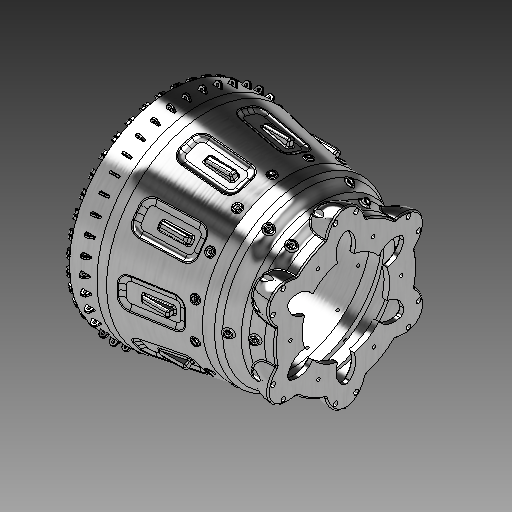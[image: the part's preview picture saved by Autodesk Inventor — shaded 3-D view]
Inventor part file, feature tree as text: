
AUTODESK INVENTOR PART (.ipt)
format: ipt  version: 2019 (Build 230136000, 136)  size: 8,577,024 bytes
history: native  units: mm
features: sketch x16, fillet x11, extrude x9, pattern_circular x9, hole x8, plane x7, other x6, revolve x1, sweep x1, delete_face x1, mirror x1, emboss x1, chamfer x1, projected_geometry x1
ambient origin geometry x8: Origin, YZ Plane, XZ Plane, XY Plane, X Axis, Y Axis, Z Axis, Center Point
bodies: Solid2 (feature_tree)
feature tree (73):
  other  "Blocks"
  sketch  "Sketch2"  dims[d2=6.0mm d3=12.566371mm]
  revolve  "Revolution1"  [1 undecoded]
  extrude  "Extrusion1"  Depth=12.0mm
  sketch  "Sketch22"  dims[d66=-6.1mm d67=4.75mm d68=0.0mm d69=-6.716mm d70=3.0mm d71=0.0mm]
  sketch  "Sketch23"  dims[d76=400.0mm d77=360.0deg d79=-139.973mm d80=40.0mm]
  sweep  "Sweep2"
  delete_face  "Delete Face7"
  plane  "Work Plane29"
  sketch  "Sketch15"  dims[d30=8.0mm d31=0.0mm]
  extrude  "Extrusion10"  Depth=121.0mm
  hole  "Hole6"  [1 undecoded]
  hole  "Hole7"  [1 undecoded]
  fillet  "Fillet14"  Radius=98.0mm
  pattern_circular  "Circular Pattern1"  Count=6 Angle=360.0deg
  plane  "Work Plane1"
  extrude  "Extrusion2"  Depth=3.0mm TaperAngle=0.0deg
  fillet  "Fillet1"  Radius=4.0mm
  pattern_circular  "Circular Pattern2"  Count=40 Angle=360.0deg
  sketch  "Sketch8"  dims[d9=16.0mm d10=121.0mm]
  plane  "Work Plane5"
  plane  "Work Plane6"
  extrude  "Extrusion4"  Depth=3.0mm TaperAngle=0.0deg
  extrude  "Extrusion3"  [1 undecoded]
  fillet  "Fillet18"  Radius=40.0mm
  pattern_circular  "Circular Pattern4"  [2 undecoded]
  mirror  "Mirror3"
  sketch  "Sketch11"  dims[d17=29.779484mm d18=6.0mm d19=98.0mm]
  plane  "Work Plane10"
  emboss  "Emboss3"
  fillet  "Fillet3"  Radius=2.0mm
  fillet  "Fillet4"  Radius=2.0mm
  pattern_circular  "Circular Pattern14"  [2 undecoded]
  plane  "Work Plane9"
  sketch  "Sketch9"  dims[d11=33.5mm d12=75.0mm]
  extrude  "Extrusion6"  Depth=10.0mm
  fillet  "Fillet20"  Radius=2.0mm
  pattern_circular  "Circular Pattern6"  [2 undecoded]
  hole  "HolePlaneOnSideFace"  [1 undecoded]
  fillet  "Fillet21"  Radius=2.0mm
  extrude  "Extrusion7"  Depth=10.0mm TaperAngle=0.0deg
  hole  "HolePlane2"  [1 undecoded]
  hole  "Hole2"  [1 undecoded]
  fillet  "Fillet6"  Radius=30.0mm
  pattern_circular  "Circular Pattern7"  [2 undecoded]
  sketch  "Sketch19"  dims[d48=0.0mm d49=3.0mm d50=0.0mm d51=4.0mm]
  other  "BottonExtrudePlane1"
  extrude  "Extrusion8"  [1 undecoded]
  other  "BottomHolePlane1"
  hole  "Hole4"  [1 undecoded]
  fillet  "Fillet7"  [1 undecoded]
  pattern_circular  "Circular Pattern8"  [2 undecoded]
  other  "MiddleExtrudePlane"
  extrude  "Extrusion9"  Depth=10.0mm TaperAngle=0.0deg
  fillet  "Fillet8"  Radius=0.715mm
  other  "MiddleHolePlane"
  hole  "Hole5"  [1 undecoded]
  pattern_circular  "Circular Pattern9"  [2 undecoded]
  hole  "Hole9"  [1 undecoded]
  pattern_circular  "Circular Pattern13"  [2 undecoded]
  fillet  "Fillet15"  Radius=10.0mm
  plane  "Work Plane42"
  sketch  "Sketch31"  dims[d81=10.0mm]
  chamfer  "Chamfer1"  Distance=3.0mm
  sketch  "Sketch4"  dims[d5=16.0mm d6=12.0mm]
  sketch  "Sketch6"  dims[d7=16.0mm d8=15.5mm]
  sketch  "Sketch12"  dims[d20=90.0deg]
  sketch  "Sketch17"  dims[d38=32.0mm d43=60.0mm d44=360.0deg]
  sketch  "Sketch20"  dims[d52=5.0mm]
  sketch  "Sketch21"  dims[d53=0.5mm d54=400.0mm d55=360.0deg]
  other  "Block1"
  sketch  "Sketch32"  dims[d82=2.0mm d83=2.0mm d84=2.0mm d85=2.0mm d86=2.0mm d87=2.0mm d88=2.0mm d89=2.0mm d95=10.0mm d96=2.0mm d103=3.0mm d104=0.0mm d105=100.0mm d106=360.0deg d108=2.8mm d111=30.0mm d113=6.0mm d114=-11.0mm d131=4.107mm d132=0.0mm d133=-131.011mm d135=11.0mm d137=3.0mm d138=0.0mm d149=10.0mm d150=10.0mm d141=4.117mm d142=6.0mm d143=7.53mm d144=2.0mm d145=90.0deg d146=8.0mm d147=20.594885mm d148=0.715mm d151=150.0mm d152=360.0deg d154=1.0mm d156=24.629995mm d158=68.545214mm d166=10.0mm d167=3.0mm d168=0.0mm d169=-0.715mm d170=10.0mm d171=10.0mm d172=4.117mm d173=6.0mm d174=7.53mm d175=2.0mm d176=90.0deg d177=12.0mm d178=20.594885mm d179=60.0mm d180=360.0deg d182=2.0mm d184=6.806784mm d185=10.0mm d186=3.0mm d187=0.0mm d188=2.0mm d189=0.715mm d190=10.0mm d191=10.0mm d192=4.117mm d193=6.0mm d194=7.53mm d195=2.0mm d196=90.0deg d197=12.0mm d198=20.594885mm d199=60.0mm d200=360.0deg d205=0.0mm d206=0.0mm d212=3.0mm d213=0.0mm d271=10.0mm d272=10.0mm d216=7.0mm d217=6.0mm d218=7.53mm d219=2.0mm d220=90.0deg d221=12.0mm d222=20.594885mm d258=10.0mm d259=10.0mm d225=7.0mm d226=6.0mm d227=7.53mm d228=2.0mm d229=90.0deg d230=12.0mm d231=20.594885mm d234=2.0mm d244=10.0mm d245=15.0mm d246=114.422291mm d251=10.0mm d252=114.422mm d253=15.0mm d273=2.0mm d298=-369.5mm d318=0.25mm d363=208.0mm d366=89.0mm d374=8.0mm d377=28.0mm d378=60.0mm d380=360.0deg d382=64.0mm d383=12.0mm d384=2.0mm d385=2.0mm d386=45.0deg d387=190.0mm d389=7.0mm d390=17.0mm d391=10.0mm d392=13.0mm d393=40.0mm d394=2.2mm d395=5.6mm d396=8.6mm d400=10.0mm d401=14.0mm d402=390.0mm d403=85.0mm d404=45.0mm d407=41.0mm d408=70.0mm d409=5.0mm d410=6.0mm d411=4.0mm d412=2.0mm d413=90.0deg d414=8.0mm d415=20.594885mm d416=60.0mm d417=360.0deg d419=407.5mm d420=15.0mm d421=7.6mm d422=5.0mm d423=145.5mm d424=11.519173mm d425=303.0mm d426=100.0mm d427=360.0deg d431=258.0mm d432=3.0mm d433=2.0mm d434=25.0mm]
  projected_geometry  "Project Cut Edges5"
note: 26 required parameter values undecoded (feature->parameter linkage not recoverable at this tier; creation-order binding heuristic only, values carry confidence <= 0.55)